# Revit family: LAMP_PUZZLE TRP
name_source: partatom
category: Modelos genéricos
revit_build: Autodesk Revit 2015 (Build: 20140606_1530(x64)
units: mm (PartAtom-declared; Revit-internal decimal feet)

## types (24) — shared parameters
CRI = 80
Comentarios de tipo = Availability of tilting between -25º and 25º in both directions when placed in a project.
Dimensions = 450 x 140 x 139
Elevación por defecto = 1219 mm
Fabricante = LAMP
Gear = Electronic
Height = 139 mm  [stored 0.456037 ft]
Installation instructions = http://www.lamp.es
Insulation class = II
Lamp = COB LED
Last update = 24/07/2018
Luminaire type = Indoor - Recessed luminaire
MacAdam = 3
Manufacturer URL = http://www.lamp.es
Manufacturer country = Spain
Manufacturer name = LAMP
Model explanation = Availability of tilting between -25º and 25º in both directions when placed in a project.
Power Supply = 220-240V 50-60Hz
Product URL = http://www.lamp.es
Product datasheet = http://www.lamp.es
Protection rating = IP20
Type = COB PHILIPS

## per-type parameters (varying)
| type | Descripción | Efficacy | Finish | IEE | Initial color | Initial intensity | LED Lifetime | Material caja | Modelo | Photometric web file 1 | Photometric web file 2 | Photometric web file 3 | Plum | Power | Product code | Weight |
| 7032LM 3000 BLACK FLOOD | PUZZLE G2 TRP 2500 WW FL BK. | 124 lm/W | Matte black | A++ | 3000 K | 7032 lm | 50.000 L80 B10 | LAMP_Aluminio aro Puzzle BL | PU2RE325FL830NB | Aro exterior : 2344LM 3000 BLACK FLOOD | Aro exterior : 2344LM 3000 BLACK FLOOD | Aro exterior : 2344LM 3000 BLACK FLOOD | 57 W | 54 W | PU2RE325FL830NB | 3.04 kg |
| 7032LM 3000 WHITE FLOOD | PUZZLE G2 TRP 2500 WW FL WH. | 124 lm/W | Matte white | A++ | 3000 K | 7032 lm | 50.000 L80 B10 | LAMP_Aluminio aro Puzzle WH | PU2RE325FL830NW | Aro exterior : 2344LM 3000 WHITE FLOOD | Aro exterior : 2344LM 3000 WHITE FLOOD | Aro exterior : 2344LM 3000 WHITE FLOOD | 57 W | 54 W | PU2RE325FL830NW | 3.04 kg |
| 7104LM 3000 BLACK MEDIUM FLOOD | PUZZLE G2 TRP 2500 WW MFL BK. | 125 lm/W | Matte black | A++ | 3000 K | 7104 lm | 50.000 L80 B10 | LAMP_Aluminio aro Puzzle BL | PU2RE325MF830NB | Aro exterior : 2368LM 3000 BLACK MEDIUM FLOOD | Aro exterior : 2368LM 3000 BLACK MEDIUM FLOOD | Aro exterior : 2368LM 3000 BLACK MEDIUM FLOOD | 57 W | 54 W | PU2RE325MF830NB | 3.04 kg |
| 7104LM 3000 WHITE MEDIUM FLOOD | PUZZLE G2 TRP 2500 WW MFL WH. | 125 lm/W | Matte white | A++ | 3000 K | 7104 lm | 50.000 L80 B10 | LAMP_Aluminio aro Puzzle WH | PU2RE325MF830NW | Aro exterior : 2368LM 3000 WHITE MEDIUM FLOOD | Aro exterior : 2368LM 3000 WHITE MEDIUM FLOOD | Aro exterior : 2368LM 3000 WHITE MEDIUM FLOOD | 57 W | 54 W | PU2RE325MF830NW | 3.04 kg |
| 7326LM 4000 BLACK FLOOD | PUZZLE G2 TRP 2500 NW FL BK. | 129 lm/W | Matte black | A++ | 4000 K | 7326 lm | 50.000 L80 B10 | LAMP_Aluminio aro Puzzle BL | PU2RE325FL840NB | Aro exterior : 2442LM 4000 BLACK FLOOD | Aro exterior : 2442LM 4000 BLACK FLOOD | Aro exterior : 2442LM 4000 BLACK FLOOD | 57 W | 54 W | PU2RE325FL840NB | 3.04 kg |
| 7326LM 4000 WHITE FLOOD | PUZZLE G2 TRP 2500 NW FL WH. | 129 lm/W | Matte white | A++ | 4000 K | 7326 lm | 50.000 L80 B10 | LAMP_Aluminio aro Puzzle WH | PU2RE325FL840NW | Aro exterior : 2442LM 4000 WHITE FLOOD | Aro exterior : 2442LM 4000 WHITE FLOOD | Aro exterior : 2442LM 4000 WHITE FLOOD | 57 W | 54 W | PU2RE325FL840NW | 3.04 kg |
| 7398LM 4000 BLACK MEDIUM FLOOD | PUZZLE G2 TRP 2500 NW MFL BK. | 131 lm/W | Matte black | A++ | 4000 K | 7398 lm | 50.000 L80 B10 | LAMP_Aluminio aro Puzzle BL | PU2RE325MF840NB | Aro exterior : 2466LM 4000 BLACK MEDIUM FLOOD | Aro exterior : 2466LM 4000 BLACK MEDIUM FLOOD | Aro exterior : 2466LM 4000 BLACK MEDIUM FLOOD | 57 W | 54 W | PU2RE325MF840NB | 3.04 kg |
| 7398LM 4000 WHITE MEDIUM FLOOD | PUZZLE G2 TRP 2500 NW MFL WH. | 131 lm/W | Matte white | A++ | 4000 K | 7398 lm | 50.000 L80 B10 | LAMP_Aluminio aro Puzzle WH | PU2RE325MF840NW | Aro exterior : 2466LM 4000 WHITE MEDIUM FLOOD | Aro exterior : 2466LM 4000 WHITE MEDIUM FLOOD | Aro exterior : 2466LM 4000 WHITE MEDIUM FLOOD | 57 W | 54 W | PU2RE325MF840NW | 3.04 kg |
| 9591LM 3000 BLACK FLOOD | PUZZLE G2 TRP 3500 WW FL BK. | 97 lm/W | Matte black | A+ | 3000 K | 9591 lm | 50.000 L70 B10 | LAMP_Aluminio aro Puzzle BL | PU2RE335FL830NB | Aro exterior : 3197LM 3000 BLACK FLOOD | Aro exterior : 3197LM 3000 BLACK FLOOD | Aro exterior : 3197LM 3000 BLACK FLOOD | 99 W | 87 W | PU2RE335FL830NB | 3.19 kg |
| 9591LM 3000 WHITE FLOOD | PUZZLE G2 TRP 3500 WW FL WH. | 97 lm/W | Matte white | A+ | 3000 K | 9591 lm | 50.000 L70 B10 | LAMP_Aluminio aro Puzzle WH | PU2RE335FL830NW | Aro exterior : 3197LM 3000 WHITE FLOOD | Aro exterior : 3197LM 3000 WHITE FLOOD | Aro exterior : 3197LM 3000 WHITE FLOOD | 99 W | 87 W | PU2RE335FL830NW | 3.19 kg |
| 9687LM 3000 BLACK MEDIUM FLOOD | PUZZLE G2 TRP 3500 WW MFL BK. | 98 lm/W | Matte black | A+ | 3000 K | 9687 lm | 50.000 L70 B10 | LAMP_Aluminio aro Puzzle BL | PU2RE335MF830NB | Aro exterior : 3229LM 3000 BLACK MEDIUM FLOOD | Aro exterior : 3229LM 3000 BLACK MEDIUM FLOOD | Aro exterior : 3229LM 3000 BLACK MEDIUM FLOOD | 99 W | 87 W | PU2RE335MF830NB | 3.19 kg |
| 9687LM 3000 WHITE MEDIUM FLOOD | PUZZLE G2 TRP 3500 WW MFL WH. | 98 lm/W | Matte white | A+ | 3000 K | 9687 lm | 50.000 L70 B10 | LAMP_Aluminio aro Puzzle WH | PU2RE335MF830NW | Aro exterior : 3229LM 3000 WHITE MEDIUM FLOOD | Aro exterior : 3229LM 3000 WHITE MEDIUM FLOOD | Aro exterior : 3229LM 3000 WHITE MEDIUM FLOOD | 99 W | 87 W | PU2RE335MF830NW | 3.19 kg |
| 9990LM 4000 BLACK FLOOD | PUZZLE G2 TRP 3500 NW FL BK. | 101 lm/W | Matte black | A+ | 4000 K | 9990 lm | 50.000 L70 B10 | LAMP_Aluminio aro Puzzle BL | PU2RE335FL840NB | Aro exterior : 3330LM 4000 BLACK FLOOD | Aro exterior : 3330LM 4000 BLACK FLOOD | Aro exterior : 3330LM 4000 BLACK FLOOD | 99 W | 87 W | PU2RE335FL840NB | 3.19 kg |
| 9990LM 4000 WHITE FLOOD | PUZZLE G2 TRP 3500 NW FL WH. | 101 lm/W | Matte white | A+ | 4000 K | 9990 lm | 50.000 L70 B10 | LAMP_Aluminio aro Puzzle WH | PU2RE335FL840NW | Aro exterior : 3330LM 4000 WHITE FLOOD | Aro exterior : 3330LM 4000 WHITE FLOOD | Aro exterior : 3330LM 4000 WHITE FLOOD | 99 W | 87 W | PU2RE335FL840NW | 3.19 kg |
| 10089LM 4000 BLACK MEDIUM FLOOD | PUZZLE G2 TRP 3500 NW MFL BK. | 102 lm/W | Matte black | A+ | 4000 K | 10089 lm | 50.000 L70 B10 | LAMP_Aluminio aro Puzzle BL | PU2RE335MF840NB | Aro exterior : 3363LM 4000 BLACK MEDIUM FLOOD | Aro exterior : 3363LM 4000 BLACK MEDIUM FLOOD | Aro exterior : 3363LM 4000 BLACK MEDIUM FLOOD | 99 W | 87 W | PU2RE335MF840NB | 3.19 kg |
| 10089LM 4000 WHITE MEDIUM FLOOD | PUZZLE G2 TRP 3500 NW MFL WH. | 102 lm/W | Matte white | A+ | 4000 K | 10089 lm | 50.000 L70 B10 | LAMP_Aluminio aro Puzzle WH | PU2RE335MF840NW | Aro exterior : 3363LM 4000 WHITE MEDIUM FLOOD | Aro exterior : 3363LM 4000 WHITE MEDIUM FLOOD | Aro exterior : 3363LM 4000 WHITE MEDIUM FLOOD | 99 W | 87 W | PU2RE335MF840NW | 3.19 kg |
| 12153LM 3000 BLACK MEDIUM FLOOD | PUZZLE G2 TRP 4600 WW MFL BK. | 106 lm/W | Matte black | A+ | 3000 K | 12153 lm | 50.000 L80 B10 | LAMP_Aluminio aro Puzzle BL | PU2RE345MF830NB | Aro exterior : 4051LM 3000 BLACK MEDIUM FLOOD | Aro exterior : 4051LM 3000 BLACK MEDIUM FLOOD | Aro exterior : 4051LM 3000 BLACK MEDIUM FLOOD | 115 W | 99 W | PU2RE345MF830NB | 3.43 kg |
| 12153LM 3000 WHITE MEDIUM FLOOD | PUZZLE G2 TRP 4600 WW MFL WH. | 106 lm/W | Matte white | A+ | 3000 K | 12153 lm | 50.000 L80 B10 | LAMP_Aluminio aro Puzzle WH | PU2RE345MF830NW | Aro exterior : 4051LM 3000 WHITE MEDIUM FLOOD | Aro exterior : 4051LM 3000 WHITE MEDIUM FLOOD | Aro exterior : 4051LM 3000 WHITE MEDIUM FLOOD | 115 W | 99 W | PU2RE345MF830NW | 3.43 kg |
| 12411LM 3000 BLACK FLOOD | PUZZLE G2 TRP 4600 WW FL BK. | 108 lm/W | Matte black | A+ | 3000 K | 12411 lm | 50.000 L80 B10 | LAMP_Aluminio aro Puzzle BL | PU2RE345FL830NB | Aro exterior : 4137LM 3000 BLACK FLOOD | Aro exterior : 4137LM 3000 BLACK FLOOD | Aro exterior : 4137LM 3000 BLACK FLOOD | 115 W | 99 W | PU2RE345FL830NB | 3.43 kg |
| 12411LM 3000 WHITE FLOOD | PUZZLE G2 TRP 4600 WW FL WH. | 108 lm/W | Matte white | A+ | 3000 K | 12411 lm | 50.000 L80 B10 | LAMP_Aluminio aro Puzzle WH | PU2RE345FL830NW | Aro exterior : 4137LM 3000 WHITE FLOOD | Aro exterior : 4137LM 3000 WHITE FLOOD | Aro exterior : 4137LM 3000 WHITE FLOOD | 115 W | 99 W | PU2RE345FL830NW | 3.43 kg |
| 12660LM 4000 BLACK MEDIUM FLOOD | PUZZLE G2 TRP 4600 NW MFL BK. | 111 lm/W | Matte black | A+ | 4000 K | 12660 lm | 50.000 L80 B10 | LAMP_Aluminio aro Puzzle BL | PU2RE345MF840NB | Aro exterior : 4220LM 4000 BLACK MEDIUM FLOOD | Aro exterior : 4220LM 4000 BLACK MEDIUM FLOOD | Aro exterior : 4220LM 4000 BLACK MEDIUM FLOOD | 115 W | 99 W | PU2RE345MF840NB | 3.43 kg |
| 12660LM 4000 WHITE MEDIUM FLOOD | PUZZLE G2 TRP 4600 NW MFL WH. | 111 lm/W | Matte white | A+ | 4000 K | 12660 lm | 50.000 L80 B10 | LAMP_Aluminio aro Puzzle WH | PU2RE345MF840NW | Aro exterior : 4220LM 4000 WHITE MEDIUM FLOOD | Aro exterior : 4220LM 4000 WHITE MEDIUM FLOOD | Aro exterior : 4220LM 4000 WHITE MEDIUM FLOOD | 115 W | 99 W | PU2RE345MF840NW | 3.43 kg |
| 12927LM 4000 BLACK FLOOD | PUZZLE G2 TRP 4600 NW FL BK. | 113 lm/W | Matte black | A+ | 4000 K | 12927 lm | 50.000 L80 B10 | LAMP_Aluminio aro Puzzle BL | PU2RE345FL840NB | Aro exterior : 4309LM 4000 BLACK FLOOD | Aro exterior : 4309LM 4000 BLACK FLOOD | Aro exterior : 4309LM 4000 BLACK FLOOD | 115 W | 99 W | PU2RE345FL840NB | 3.43 kg |
| 12927LM 4000 WHITE FLOOD | PUZZLE G2 TRP 4600 NW FL WH. | 113 lm/W | Matte white | A+ | 4000 K | 12927 lm | 50.000 L80 B10 | LAMP_Aluminio aro Puzzle WH | PU2RE345FL840NW | Aro exterior : 4309LM 4000 WHITE FLOOD | Aro exterior : 4309LM 4000 WHITE FLOOD | Aro exterior : 4309LM 4000 WHITE FLOOD | 115 W | 99 W | PU2RE345FL840NW | 3.43 kg |

note: [stored X ft] marks values corroborated as IEEE doubles in the binary element streams (Revit-internal decimal feet)
